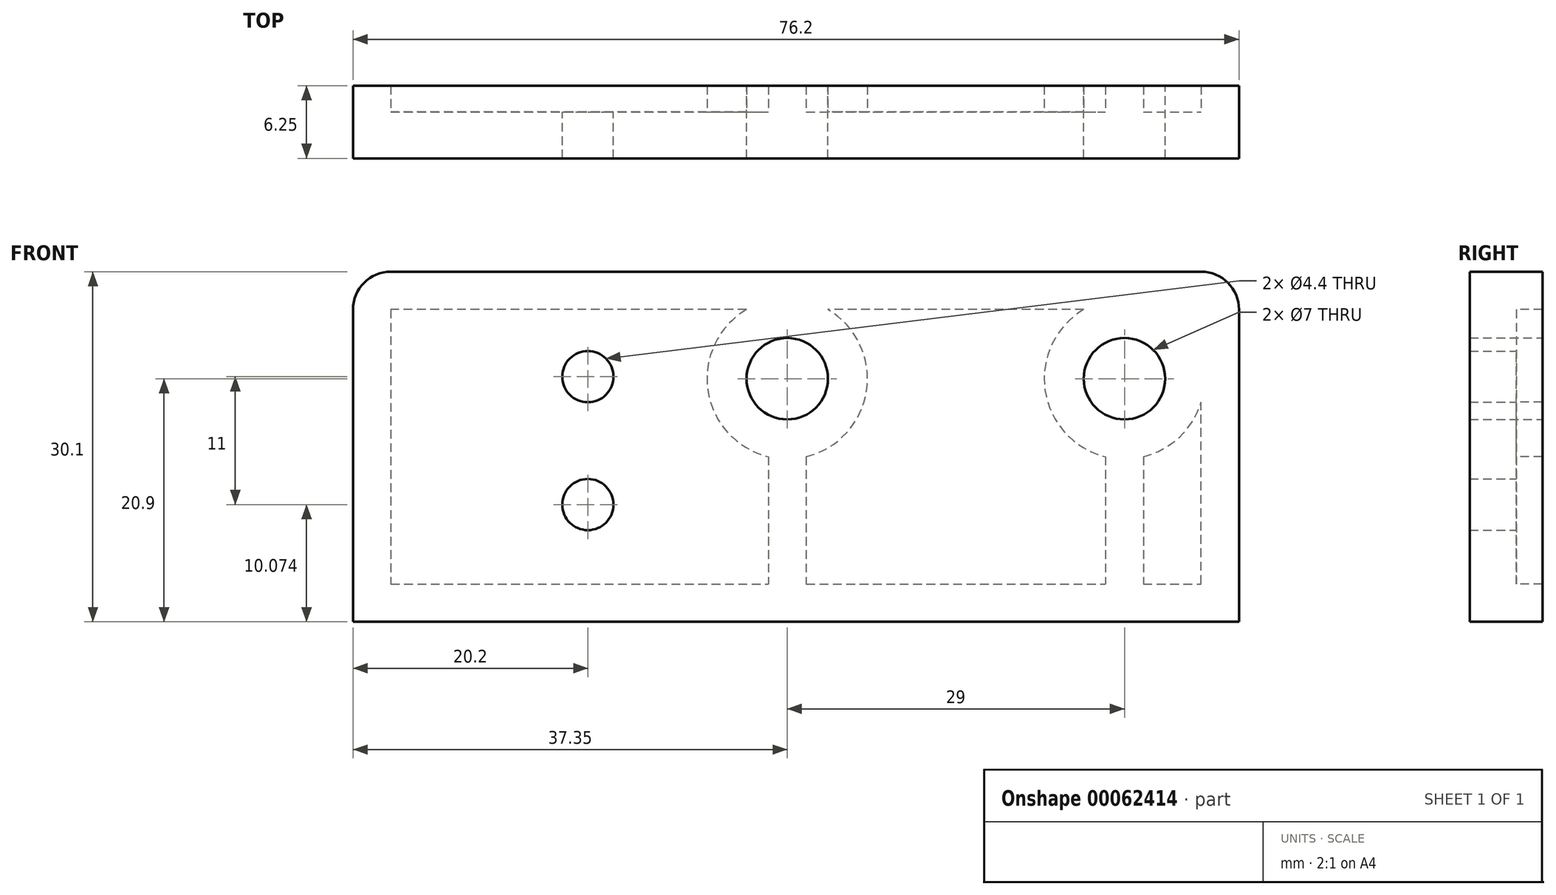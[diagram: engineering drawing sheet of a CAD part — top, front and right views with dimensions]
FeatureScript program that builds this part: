
annotation { "Feature Type Name" : "Feature", "Feature Type Description" : "" }
export const myFeature = defineFeature(function(context is Context, id is Id, definition is map)
    precondition{}
    {
        {
            var Q0;
            Q0=qCreatedBy(makeId("Front.planeOp"),FACE);
            var sketch = newSketch(context, id + "F0", { "sketchPlane" : qUnion([Q0])});
            skLineSegment(sketch, "E0.bottom", {"start": v(-38.1, 0) * mm, "end": v(38.1, 0) * mm});
            skCircle(sketch, "E1", {"center": v(-17.9, 10.07) * mm, "radius": 2.2 * mm});
            skCircle(sketch, "E2", {"center": v(-17.9, 21.07) * mm, "radius": 2.2 * mm});
            skLineSegment(sketch, "E3", {"start": v(38.1, 0) * mm, "end": v(38.1, 26.85) * mm});
            skLineSegment(sketch, "E4", {"start": v(34.85, 30.1) * mm, "end": v(-34.85, 30.1) * mm});
            skLineSegment(sketch, "E5", {"start": v(-38.1, 26.85) * mm, "end": v(-38.1, 0) * mm});
            skCircle(sketch, "E6", {"center": v(28.25, 20.9) * mm, "radius": 3.5 * mm});
            skCircle(sketch, "E7", {"center": v(-0.75, 20.9) * mm, "radius": 3.5 * mm});
            skPoint(sketch, "E8.visualSharp", {"position": v(-38.1, 30.1) * mm});
            skArc(sketch, "E8.filletArc", {"start": v(-34.85, 30.1) * mm, "mid": v(-37.15, 29.15) * mm, "end": v(-38.1, 26.85) * mm});
            skPoint(sketch, "E9.visualSharp", {"position": v(38.1, 30.1) * mm});
            skArc(sketch, "E9.filletArc", {"start": v(38.1, 26.85) * mm, "mid": v(37.15, 29.15) * mm, "end": v(34.85, 30.1) * mm});
            skCircle(sketch, "E10", {"center": v(-0.75, 20.9) * mm, "radius": 6.9 * mm});
            skCircle(sketch, "E11", {"center": v(28.25, 20.9) * mm, "radius": 6.9 * mm});
            skLineSegment(sketch, "E12.0", {"start": v(-34.85, 26.85) * mm, "end": v(-34.85, 3.25) * mm});
            skLineSegment(sketch, "E12.1", {"start": v(-34.85, 26.85) * mm, "end": v(-34.85, 26.85) * mm});
            skLineSegment(sketch, "E12.2", {"start": v(34.85, 26.85) * mm, "end": v(-34.85, 26.85) * mm});
            skLineSegment(sketch, "E12.3", {"start": v(34.85, 26.85) * mm, "end": v(34.85, 26.85) * mm});
            skLineSegment(sketch, "E12.4", {"start": v(34.85, 3.25) * mm, "end": v(34.85, 26.85) * mm});
            skLineSegment(sketch, "E12.5", {"start": v(-34.85, 3.25) * mm, "end": v(34.85, 3.25) * mm});
            skLineSegment(sketch, "E13", {"start": v(-2.38, 14.2) * mm, "end": v(-2.38, 3.25) * mm});
            skLineSegment(sketch, "E14", {"start": v(0.88, 14.2) * mm, "end": v(0.88, 3.25) * mm});
            skLineSegment(sketch, "E15", {"start": v(26.62, 14.2) * mm, "end": v(26.62, 3.25) * mm});
            skLineSegment(sketch, "E16", {"start": v(29.88, 14.2) * mm, "end": v(29.88, 3.25) * mm});
            skLineSegment(sketch, "E17", {"start": v(-2.38, 8.72) * mm, "end": v(0.88, 8.72) * mm, "construction": true});
            skLineSegment(sketch, "E18", {"start": v(26.62, 8.72) * mm, "end": v(29.88, 8.72) * mm, "construction": true});
            skLineSegment(sketch, "E19", {"start": v(-0.75, 8.72) * mm, "end": v(-0.75, 20.9) * mm, "construction": true});
            skLineSegment(sketch, "E20", {"start": v(28.25, 8.72) * mm, "end": v(28.25, 20.9) * mm, "construction": true});
            skSolve(sketch);
        }
        {
            var Q0;
            {var subQ4=sQuery(id+"F0.wireOp",EDGE,"E14");var subQ9=sQuery(id+"F0.wireOp",EDGE,"E10");var subQ10=makeQuery(id+"F0.imprint","INTERSECT",VERTEX,{"derivedFrom":[subQ9,subQ4]});Q0=makeQuery(id+"F0.imprint","IMPRINT",FACE,{"disambiguationData":[TD([[makeQuery(id+"F0.imprint","IMPRINT",EDGE,{"disambiguationData":[TD([[subQ10,-1.0]])],"derivedFrom":subQ9}),-1.0]])]});}
            var Q1;
            {var subQ0=sQuery(id+"F0.wireOp",EDGE,"E16");var subQ4=sQuery(id+"F0.wireOp",EDGE,"E11");var subQ5=makeQuery(id+"F0.imprint","INTERSECT",VERTEX,{"derivedFrom":[subQ4,subQ0]});Q1=makeQuery(id+"F0.imprint","IMPRINT",FACE,{"disambiguationData":[TD([[makeQuery(id+"F0.imprint","IMPRINT",EDGE,{"disambiguationData":[TD([[subQ5,-1.0]])],"derivedFrom":subQ4}),-1.0]])]});}
            var Q2;
            {var subQ1=sQuery(id+"F0.wireOp",EDGE,"E11");var subQ3=sQuery(id+"F0.wireOp",EDGE,"E12.2");var subQ5=makeQuery(id+"F0.imprint","INTERSECT",VERTEX,{"disambiguationData":[OD(0.0)],"derivedFrom":[subQ1,subQ3]});Q2=makeQuery(id+"F0.imprint","IMPRINT",FACE,{"disambiguationData":[TD([[makeQuery(id+"F0.imprint","IMPRINT",EDGE,{"disambiguationData":[TD([[subQ5,1.0]])],"derivedFrom":subQ1}),-1.0]])]});}
            var Q3;
            Q3=makeQuery(id+"F0.imprint","IMPRINT",FACE,{"disambiguationData":[TD([[makeQuery(id+"F0.imprint","IMPRINT",EDGE,{"derivedFrom":sQuery(id+"F0.wireOp",EDGE,"E0.bottom")}),1.0]])]});
            var Q4;
            Q4=makeQuery(id+"F0.imprint","IMPRINT",FACE,{"disambiguationData":[TD([[makeQuery(id+"F0.imprint","IMPRINT",EDGE,{"derivedFrom":sQuery(id+"F0.wireOp",EDGE,"E6")}),-1.0]])]});
            var Q5;
            {var subQ1=sQuery(id+"F0.wireOp",EDGE,"E11");var subQ5=sQuery(id+"F0.wireOp",EDGE,"E15");var subQ7=makeQuery(id+"F0.imprint","INTERSECT",VERTEX,{"derivedFrom":[subQ1,subQ5]});Q5=makeQuery(id+"F0.imprint","IMPRINT",FACE,{"disambiguationData":[TD([[makeQuery(id+"F0.imprint","IMPRINT",EDGE,{"disambiguationData":[TD([[subQ7,-1.0]])],"derivedFrom":subQ1}),-1.0]])]});}
            var Q6;
            {var subQ3=sQuery(id+"F0.wireOp",EDGE,"E16");var subQ5=sQuery(id+"F0.wireOp",EDGE,"E11");var subQ7=makeQuery(id+"F0.imprint","INTERSECT",VERTEX,{"derivedFrom":[subQ5,subQ3]});Q6=makeQuery(id+"F0.imprint","IMPRINT",FACE,{"disambiguationData":[TD([[makeQuery(id+"F0.imprint","IMPRINT",EDGE,{"disambiguationData":[TD([[subQ7,1.0]])],"derivedFrom":subQ5}),-1.0]])]});}
            var Q7;
            {var subQ4=sQuery(id+"F0.wireOp",EDGE,"E12.5");var subQ6=sQuery(id+"F0.wireOp",EDGE,"E15");var subQ8=makeQuery(id+"F0.imprint","INTERSECT",VERTEX,{"derivedFrom":[subQ4,subQ6]});Q7=makeQuery(id+"F0.imprint","IMPRINT",FACE,{"disambiguationData":[TD([[makeQuery(id+"F0.imprint","IMPRINT",EDGE,{"disambiguationData":[TD([[subQ8,-1.0]])],"derivedFrom":subQ4}),1.0]])]});}
            var Q8;
            {var subQ4=sQuery(id+"F0.wireOp",EDGE,"E13");var subQ6=sQuery(id+"F0.wireOp",EDGE,"E12.5");var subQ8=makeQuery(id+"F0.imprint","INTERSECT",VERTEX,{"derivedFrom":[subQ6,subQ4]});Q8=makeQuery(id+"F0.imprint","IMPRINT",FACE,{"disambiguationData":[TD([[makeQuery(id+"F0.imprint","IMPRINT",EDGE,{"disambiguationData":[TD([[subQ8,-1.0]])],"derivedFrom":subQ6}),1.0]])]});}
            var Q9;
            {var subQ1=sQuery(id+"F0.wireOp",EDGE,"E10");var subQ5=sQuery(id+"F0.wireOp",EDGE,"E14");var subQ7=makeQuery(id+"F0.imprint","INTERSECT",VERTEX,{"derivedFrom":[subQ1,subQ5]});Q9=makeQuery(id+"F0.imprint","IMPRINT",FACE,{"disambiguationData":[TD([[makeQuery(id+"F0.imprint","IMPRINT",EDGE,{"disambiguationData":[TD([[subQ7,1.0]])],"derivedFrom":subQ1}),-1.0]])]});}
            var Q10;
            {var subQ1=sQuery(id+"F0.wireOp",EDGE,"E10");var subQ5=sQuery(id+"F0.wireOp",EDGE,"E13");var subQ7=makeQuery(id+"F0.imprint","INTERSECT",VERTEX,{"derivedFrom":[subQ1,subQ5]});Q10=makeQuery(id+"F0.imprint","IMPRINT",FACE,{"disambiguationData":[TD([[makeQuery(id+"F0.imprint","IMPRINT",EDGE,{"disambiguationData":[TD([[subQ7,-1.0]])],"derivedFrom":subQ1}),-1.0]])]});}
            var Q11;
            Q11=makeQuery(id+"F0.imprint","IMPRINT",FACE,{"disambiguationData":[TD([[makeQuery(id+"F0.imprint","IMPRINT",EDGE,{"derivedFrom":sQuery(id+"F0.wireOp",EDGE,"E7")}),-1.0]])]});
            var Q12;
            {var subQ0=sQuery(id+"F0.wireOp",EDGE,"E12.2");var subQ1=sQuery(id+"F0.wireOp",EDGE,"E10");var subQ3=makeQuery(id+"F0.imprint","INTERSECT",VERTEX,{"disambiguationData":[OD(0.0)],"derivedFrom":[subQ1,subQ0]});Q12=makeQuery(id+"F0.imprint","IMPRINT",FACE,{"disambiguationData":[TD([[makeQuery(id+"F0.imprint","IMPRINT",EDGE,{"disambiguationData":[TD([[subQ3,1.0]])],"derivedFrom":subQ1}),1.0]])]});}
            var Q13;
            {var subQ0=sQuery(id+"F0.wireOp",EDGE,"E12.2");var subQ1=sQuery(id+"F0.wireOp",EDGE,"E11");var subQ3=makeQuery(id+"F0.imprint","INTERSECT",VERTEX,{"disambiguationData":[OD(0.0)],"derivedFrom":[subQ1,subQ0]});Q13=makeQuery(id+"F0.imprint","IMPRINT",FACE,{"disambiguationData":[TD([[makeQuery(id+"F0.imprint","IMPRINT",EDGE,{"disambiguationData":[TD([[subQ3,-1.0]])],"derivedFrom":subQ1}),1.0]])]});}
            var Q14;
            {var subQ0=sQuery(id+"F0.wireOp",EDGE,"E12.4");var subQ1=sQuery(id+"F0.wireOp",EDGE,"E11");var subQ3=makeQuery(id+"F0.imprint","INTERSECT",VERTEX,{"disambiguationData":[OD(0.0)],"derivedFrom":[subQ1,subQ0]});Q14=makeQuery(id+"F0.imprint","IMPRINT",FACE,{"disambiguationData":[TD([[makeQuery(id+"F0.imprint","IMPRINT",EDGE,{"disambiguationData":[TD([[subQ3,1.0]])],"derivedFrom":subQ1}),1.0]])]});}
            var Q15;
            Q15=makeQuery(id+"F0.imprint","IMPRINT",FACE,{"disambiguationData":[TD([[makeQuery(id+"F0.imprint","IMPRINT",EDGE,{"derivedFrom":sQuery(id+"F0.wireOp",EDGE,"E1")}),-1.0]])]});
            var Q16;
            {var subQ0=sQuery(id+"F0.wireOp",EDGE,"E12.2");var subQ1=sQuery(id+"F0.wireOp",EDGE,"E10");var subQ3=makeQuery(id+"F0.imprint","INTERSECT",VERTEX,{"disambiguationData":[OD(0.0)],"derivedFrom":[subQ1,subQ0]});Q16=makeQuery(id+"F0.imprint","IMPRINT",FACE,{"disambiguationData":[TD([[makeQuery(id+"F0.imprint","IMPRINT",EDGE,{"disambiguationData":[TD([[subQ3,-1.0]])],"derivedFrom":subQ1}),1.0]])]});}
            extrude(context, id + "F1", {"entities" : qUnion([Q0, Q1, Q2, Q3, Q4, Q5, Q6, Q7, Q8, Q9, Q10, Q11, Q12, Q13, Q14, Q15, Q16]), "depth" : 4 * mm});
        }
        {
            var Q0;
            Q0=makeQuery(id+"F0.imprint","IMPRINT",FACE,{"disambiguationData":[TD([[makeQuery(id+"F0.imprint","IMPRINT",EDGE,{"derivedFrom":sQuery(id+"F0.wireOp",EDGE,"E0.bottom")}),1.0]])]});
            var Q1;
            Q1=makeQuery(id+"F0.imprint","IMPRINT",FACE,{"disambiguationData":[TD([[makeQuery(id+"F0.imprint","IMPRINT",EDGE,{"derivedFrom":sQuery(id+"F0.wireOp",EDGE,"E6")}),-1.0]])]});
            var Q2;
            Q2=makeQuery(id+"F0.imprint","IMPRINT",FACE,{"disambiguationData":[TD([[makeQuery(id+"F0.imprint","IMPRINT",EDGE,{"derivedFrom":sQuery(id+"F0.wireOp",EDGE,"E7")}),-1.0]])]});
            var Q3;
            {var subQ4=sQuery(id+"F0.wireOp",EDGE,"E13");var subQ6=sQuery(id+"F0.wireOp",EDGE,"E12.5");var subQ8=makeQuery(id+"F0.imprint","INTERSECT",VERTEX,{"derivedFrom":[subQ6,subQ4]});Q3=makeQuery(id+"F0.imprint","IMPRINT",FACE,{"disambiguationData":[TD([[makeQuery(id+"F0.imprint","IMPRINT",EDGE,{"disambiguationData":[TD([[subQ8,-1.0]])],"derivedFrom":subQ6}),1.0]])]});}
            var Q4;
            {var subQ1=sQuery(id+"F0.wireOp",EDGE,"E10");var subQ5=sQuery(id+"F0.wireOp",EDGE,"E14");var subQ7=makeQuery(id+"F0.imprint","INTERSECT",VERTEX,{"derivedFrom":[subQ1,subQ5]});Q4=makeQuery(id+"F0.imprint","IMPRINT",FACE,{"disambiguationData":[TD([[makeQuery(id+"F0.imprint","IMPRINT",EDGE,{"disambiguationData":[TD([[subQ7,1.0]])],"derivedFrom":subQ1}),-1.0]])]});}
            var Q5;
            {var subQ1=sQuery(id+"F0.wireOp",EDGE,"E10");var subQ5=sQuery(id+"F0.wireOp",EDGE,"E13");var subQ7=makeQuery(id+"F0.imprint","INTERSECT",VERTEX,{"derivedFrom":[subQ1,subQ5]});Q5=makeQuery(id+"F0.imprint","IMPRINT",FACE,{"disambiguationData":[TD([[makeQuery(id+"F0.imprint","IMPRINT",EDGE,{"disambiguationData":[TD([[subQ7,-1.0]])],"derivedFrom":subQ1}),-1.0]])]});}
            var Q6;
            {var subQ1=sQuery(id+"F0.wireOp",EDGE,"E11");var subQ5=sQuery(id+"F0.wireOp",EDGE,"E15");var subQ7=makeQuery(id+"F0.imprint","INTERSECT",VERTEX,{"derivedFrom":[subQ1,subQ5]});Q6=makeQuery(id+"F0.imprint","IMPRINT",FACE,{"disambiguationData":[TD([[makeQuery(id+"F0.imprint","IMPRINT",EDGE,{"disambiguationData":[TD([[subQ7,-1.0]])],"derivedFrom":subQ1}),-1.0]])]});}
            var Q7;
            {var subQ3=sQuery(id+"F0.wireOp",EDGE,"E16");var subQ5=sQuery(id+"F0.wireOp",EDGE,"E11");var subQ7=makeQuery(id+"F0.imprint","INTERSECT",VERTEX,{"derivedFrom":[subQ5,subQ3]});Q7=makeQuery(id+"F0.imprint","IMPRINT",FACE,{"disambiguationData":[TD([[makeQuery(id+"F0.imprint","IMPRINT",EDGE,{"disambiguationData":[TD([[subQ7,1.0]])],"derivedFrom":subQ5}),-1.0]])]});}
            var Q8;
            {var subQ4=sQuery(id+"F0.wireOp",EDGE,"E12.5");var subQ6=sQuery(id+"F0.wireOp",EDGE,"E15");var subQ8=makeQuery(id+"F0.imprint","INTERSECT",VERTEX,{"derivedFrom":[subQ4,subQ6]});Q8=makeQuery(id+"F0.imprint","IMPRINT",FACE,{"disambiguationData":[TD([[makeQuery(id+"F0.imprint","IMPRINT",EDGE,{"disambiguationData":[TD([[subQ8,-1.0]])],"derivedFrom":subQ4}),1.0]])]});}
            var Q9;
            {var subQ0=sQuery(id+"F0.wireOp",EDGE,"E12.2");var subQ1=sQuery(id+"F0.wireOp",EDGE,"E10");var subQ3=makeQuery(id+"F0.imprint","INTERSECT",VERTEX,{"disambiguationData":[OD(0.0)],"derivedFrom":[subQ1,subQ0]});Q9=makeQuery(id+"F0.imprint","IMPRINT",FACE,{"disambiguationData":[TD([[makeQuery(id+"F0.imprint","IMPRINT",EDGE,{"disambiguationData":[TD([[subQ3,1.0]])],"derivedFrom":subQ1}),1.0]])]});}
            var Q10;
            {var subQ0=sQuery(id+"F0.wireOp",EDGE,"E12.2");var subQ1=sQuery(id+"F0.wireOp",EDGE,"E11");var subQ3=makeQuery(id+"F0.imprint","INTERSECT",VERTEX,{"disambiguationData":[OD(0.0)],"derivedFrom":[subQ1,subQ0]});Q10=makeQuery(id+"F0.imprint","IMPRINT",FACE,{"disambiguationData":[TD([[makeQuery(id+"F0.imprint","IMPRINT",EDGE,{"disambiguationData":[TD([[subQ3,-1.0]])],"derivedFrom":subQ1}),1.0]])]});}
            var Q11;
            {var subQ0=sQuery(id+"F0.wireOp",EDGE,"E12.4");var subQ1=sQuery(id+"F0.wireOp",EDGE,"E11");var subQ3=makeQuery(id+"F0.imprint","INTERSECT",VERTEX,{"disambiguationData":[OD(0.0)],"derivedFrom":[subQ1,subQ0]});Q11=makeQuery(id+"F0.imprint","IMPRINT",FACE,{"disambiguationData":[TD([[makeQuery(id+"F0.imprint","IMPRINT",EDGE,{"disambiguationData":[TD([[subQ3,1.0]])],"derivedFrom":subQ1}),1.0]])]});}
            var Q12;
            {var subQ1=sQuery(id+"F0.wireOp",EDGE,"E11");var subQ3=sQuery(id+"F0.wireOp",EDGE,"E12.2");var subQ5=makeQuery(id+"F0.imprint","INTERSECT",VERTEX,{"disambiguationData":[OD(0.0)],"derivedFrom":[subQ1,subQ3]});Q12=makeQuery(id+"F0.imprint","IMPRINT",FACE,{"disambiguationData":[TD([[makeQuery(id+"F0.imprint","IMPRINT",EDGE,{"disambiguationData":[TD([[subQ5,1.0]])],"derivedFrom":subQ1}),-1.0]])]});}
            extrude(context, id + "F2", {"entities" : qUnion([Q0, Q1, Q2, Q3, Q4, Q5, Q6, Q7, Q8, Q9, Q10, Q11, Q12]), "operationType" : NewBodyOperationType.ADD, "oppositeDirection" : true, "depth" : 2.25 * mm});
        }
    });
